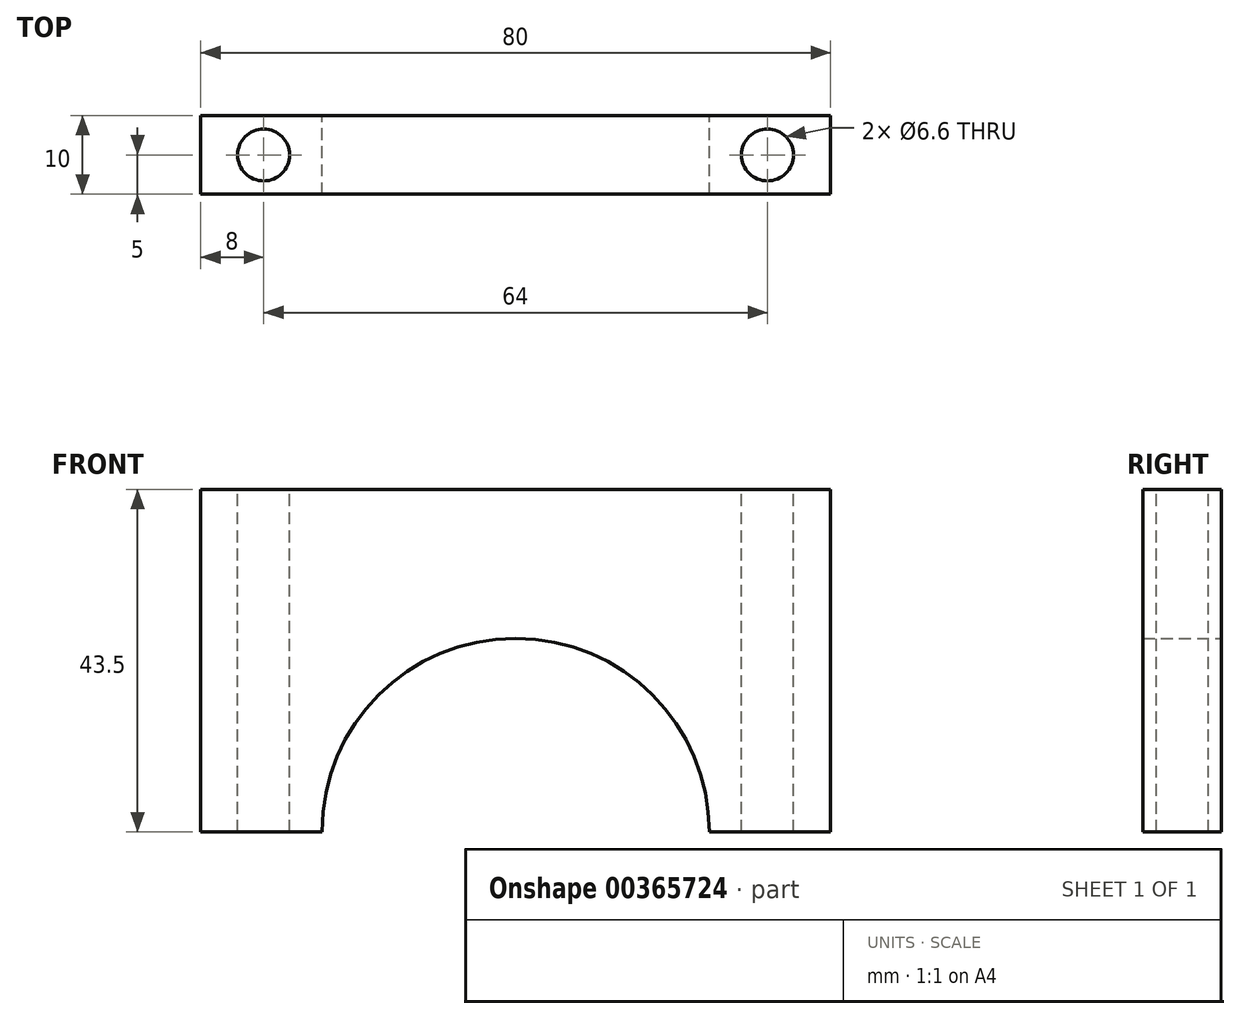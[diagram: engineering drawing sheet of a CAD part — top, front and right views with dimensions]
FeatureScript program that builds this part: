
annotation { "Feature Type Name" : "Feature", "Feature Type Description" : "" }
export const myFeature = defineFeature(function(context is Context, id is Id, definition is map)
    precondition{}
    {
        {
            var Q0;
            Q0=qCreatedBy(makeId("Front.planeOp"),FACE);
            var sketch = newSketch(context, id + "F0", { "sketchPlane" : qUnion([Q0])});
            skLineSegment(sketch, "E0.bottom", {"start": v(0, 0) * mm, "end": v(15.4, 0) * mm});
            skLineSegment(sketch, "E0.top", {"start": v(0, 43.5) * mm, "end": v(80, 43.5) * mm});
            skLineSegment(sketch, "E0.left", {"start": v(0, 0) * mm, "end": v(0, 43.5) * mm});
            skLineSegment(sketch, "E0.right", {"start": v(80, 0) * mm, "end": v(80, 43.5) * mm});
            skArc(sketch, "E1", {"start": v(64.6, 0) * mm, "mid": v(40, 24.6) * mm, "end": v(15.4, 0) * mm});
            skLineSegment(sketch, "E2.trimOffspring", {"start": v(64.6, 0) * mm, "end": v(80, 0) * mm});
            skLineSegment(sketch, "E3", {"start": v(15.4, 0) * mm, "end": v(64.6, 0) * mm, "construction": true});
            skSolve(sketch);
        }
        {
            var Q0;
            Q0 = qSketchRegion(id + "F0", true);
            extrude(context, id + "F1", {"entities" : qUnion([Q0]), "depth" : 10 * mm});
        }
        {
            var Q0;
            Q0=makeQuery(id+"F1.opExtrude","SWEPT_FACE",FACE,{"disambiguationData":[OSD([sQuery(id+"F0.wireOp",EDGE,"E0.top")])]});
            var sketch = newSketch(context, id + "F2", { "sketchPlane" : qUnion([Q0])});
            skLineSegment(sketch, "E4", {"start": v(0, -5) * mm, "end": v(80, -5) * mm, "construction": true});
            skPoint(sketch, "E5", {"position": v(8, -5) * mm});
            skPoint(sketch, "E6", {"position": v(72, -5) * mm});
            skSolve(sketch);
        }
        {
            var Q0;
            Q0=sQuery(id+"F2.wireOp",VERTEX,"E5");
            var Q1;
            Q1=sQuery(id+"F2.wireOp",VERTEX,"E6");
            var Q2;
            Q2=makeQuery(id+"F1.opExtrude","SWEPT_BODY",BODY,{"disambiguationData":[OSD([sQuery(id+"F0.wireOp",EDGE,"E0.bottom"),sQuery(id+"F0.wireOp",EDGE,"E0.top"),sQuery(id+"F0.wireOp",EDGE,"E0.left"),sQuery(id+"F0.wireOp",EDGE,"E0.right"),sQuery(id+"F0.wireOp",EDGE,"E1"),sQuery(id+"F0.wireOp",EDGE,"E2.trimOffspring")])]});
            hole(context, id + "F3", {"style" : HoleStyle.SIMPLE, "endStyle" : HoleEndStyle.THROUGH, "standardTappedOrClearance" : lookupTablePath({ "standard" : "ISO", "fit" : "Normal", "size" : "M6", "type" : "Clearance" }), "standardBlindInLast" : lookupTablePath({ "fit" : "Standard", "standard" : "ISO", "size" : "M6", "type" : "Clearance" }), "holeDiameter" : 6.6 * mm, "isTappedThrough" : true, "tappedDepth" : 12 * mm, "tapClearance" : 3, "locations" : qUnion([Q0, Q1]), "scope" : qUnion([Q2])});
        }
    });
